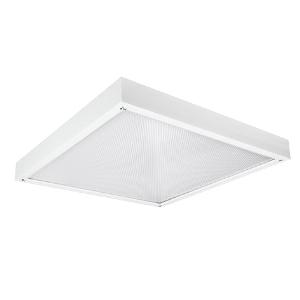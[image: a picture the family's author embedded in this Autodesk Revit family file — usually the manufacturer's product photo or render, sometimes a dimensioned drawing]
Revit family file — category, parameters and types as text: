
# Revit family: 3f_filippi_-_p_200_ip54_sp_3f_filippi_-_10859_-_p_203x10w_led_sp_ip54_596x596
name_source: partatom
category: Lighting Fixtures
units: mm (PartAtom-declared; Revit-internal decimal feet)

## family parameters
Cut with Voids When Loaded = No
Host = Face
Light Source = No
Part Type = Normal
Room Calculation Point = No
Round Connector Dimension = Use Diameter
Shared = No

## types (1)
- 3F Filippi - P 200 IP54 SP (1 x LED, 4142 lm, 34 W, 4000 K)
    Apparent Load = 34 VA
    Approval mark = ENEC
    CIE Flux Codes = 62 91 98 100 100
    Color Rendering = 80
    Color Temperature = 4000 K
    Control Gear = Electronic ballast
    Default Elevation = 1800 mm
    Description = ILLUMINOTECHNICAL
Luminous efficiency 100% (DLOR 100%, ULOR 0%).
Initial luminous flux of the luminaire 4142 lm.
Direct symmetric distribution.
Installation Interdistance Transv.D = 1.24 x hu - Long.D = 1.20 x hu.
Average luminance <3000 cd/m² for radial angles >65°.
Tabular UGR (CIE 117 - 4H-8H; S=0.25H; 70/50/20): RUG 17.8 - 17.6.
Beam angle: 92° - 92°.
Luminous efficacy 122 lm/W.
Lifetime (L93/B10): 30000 h. (tq+25°C)
Lifetime (L90/B10): 50000 h. (tq+25°C)
Lifetime (L85/B10): 80000 h. (tq+25°C)
Lifetime (L80/B10): 100000 h. (tq+25°C)
Sudden decreased luminous flux after 50000 hours: 0% (C0).
Photobiological safety in compliance with IEC/TR 62778: RG0 risk exempt, (IEC 62471).
In compliance with IEC/EN 62722-2-1 - IEC/EN 62717 standards.

SOURCE
3 linear LED modules 10W/840.
Energy efficiency class (UE 2019/2020 - UE 2019/2015): D.
CIE 13.3 Colour rendering index: CRI >80 (R9 <50%).
IES TM-30 Fidelity Index: Rf = 84 Rg = 95.
CCT nominal colour temperature 4000 K.
Colour initial tolerance (MacAdam): SDCM 2.

MECHANICAL
Housing in galvannealed steel, painted in white epoxy-polyester.
Transparent methacrylate (PMMA) flat diffuser, multilenticular exterior, anti-glare, locked to the white painted aluminium perimeter frame with sealing gasket, hinged opening.
Luminaire with limited surface temperature. - D - (EN 60598-2-24)
Dimensions: 596x596 mm, height 82 mm. Weight 5.31 kg.
IP54 protection degree.
Mechanical strength to impacts IK06 (1 joule).
Glow-wire test resistance 650°C.

ELECTRICAL
Halogen Free electronic wiring 230V-50/60Hz, power factor 0.95, THD <25%, constant output current, SELV, class I, 1 driver.
Power of the luminaire 34 W.
CE - IEC 60598-1 - EN 60598-1.
SAFE FLICKER: PstLM=<1 and SVM=<0.4 (IEC TR 61547-1 and IEC TR 63158), to ensure a more comfortable and safe light.
Luminaire compliant with EN 60598-2-22 for power supply from a centralised emergency system CPSS (Central Power Supply System), not incorporated in the luminaire - high risk areas excluded. The default power and flux are 100% in AC and 100% in DC.
Ambient temperature from 0°C to +25°C.
Temperature class T6 max 85°C.
Relative humidity UR: <85%.

INSTALLATION
Ceiling.
All accessories dedicated to this product are available on the Catalog and on our website www.3F-Filippi.com.

APPLICATIONS
Suitable product for food production plants (HACCP), IFS (Food Version 6), BRC (GSFS Food Version 7).
Environments: hospital premises, aseptic, sterilised rooms, laboratories.
Environments requiring a high level of protection, high levels of light, lamp shielding and simplified cleaning.
Environments in which there are foodstuffs or machines with moving parts, with large temperature fluctuations, and generally, in any environments that require total protection against falling fragments, SP PC version with a polycarbonate diffuser can be supplied. If necessary an L/E version i.e. with the smooth part mounted externally, or specific luminaries with laminated glass with suitable frame can also be supplied.

WARNING
Luminaire designed for disposal/recycling at end-of-life.
Replaceable (LED only) light source by a professional. Replaceable control gear by a professional.
    Height = 82 mm  [stored 0.269029 ft]
    Lamp = 1 x LED
    Lamp Light Flux = 4142 lm
    Lamp Power = 34 W
    Lamp count = 1
    Length = 596 mm
    Lifetime = 50000 h
    Luminous efficacy = 122 lm/W
    Manufacturer = 3F Filippi
    ModVariant = No
    Model = 3F Filippi - 10859 - P 203x10W LED SP IP54 596x596
    Mounting Place = Ceiling
    Mounting Type = Surface mounted
    Number of Poles = 1
    OnlyDefault = Yes
    Power Factor = 1
    Product Name = 3F Filippi - P 200 IP54 SP
    Product group = ceiling mounted luminaire
    ProductGroupID = 3
    Protection Class = Protection class I
    Protection Degree = IP 54
    RLX_Detail_Level = 1
    RLX_Emergency_Light_Flux = 0 lm
    RLX_Emergency_Type = 0
    RLX_Emergency_Type_DB = No
    RlxData = <blob elided: 39441 chars, md5=13132195>
    Socket = socket
    Standby Power = 0 W
    System Light Flux = 4142 lm
    System Power = 34 W
    Type Comments = Product without accessories
    Type Image = 3ffilippi_10859.jpg
    URL = http://relux.com
    VarID = ---
    Voltage = 0 V
    Weight = 0.00 kg
    Width = 596 mm

note: [stored X ft] marks values corroborated as IEEE doubles in the binary element streams (Revit-internal decimal feet)

## geometry (parser evidence)
native form markers: Blend x4, Sweep x10
no freeform markers — native parametric forms only
